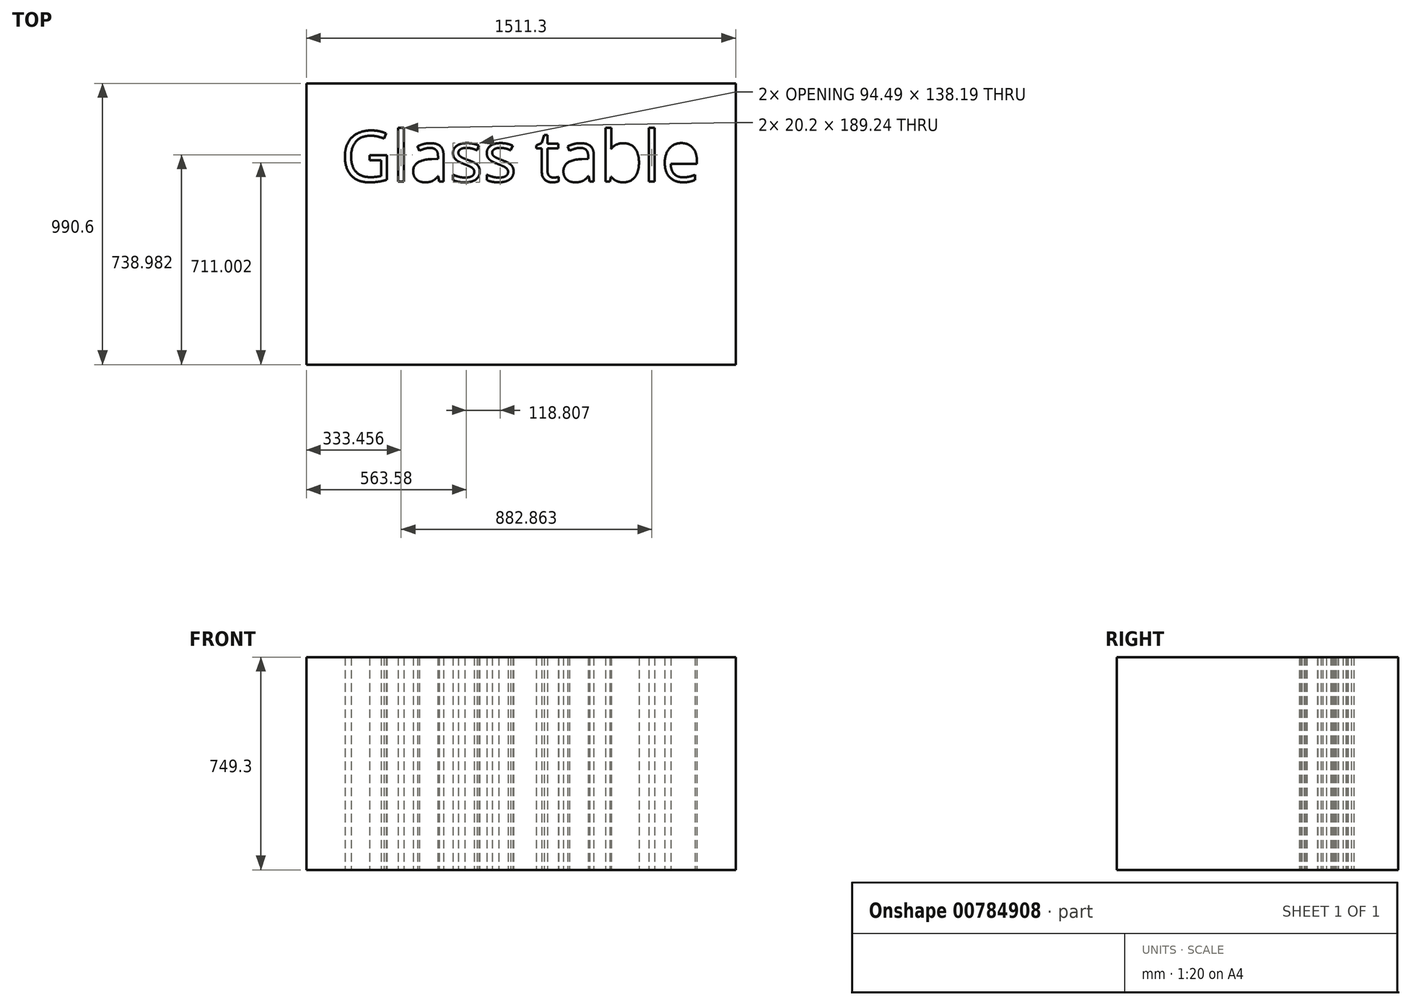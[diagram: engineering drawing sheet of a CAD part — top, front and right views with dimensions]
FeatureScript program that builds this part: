
annotation { "Feature Type Name" : "Feature", "Feature Type Description" : "" }
export const myFeature = defineFeature(function(context is Context, id is Id, definition is map)
    precondition{}
    {
        {
            var Q0;
            Q0=qCreatedBy(makeId("Top.planeOp"),FACE);
            var sketch = newSketch(context, id + "F0", { "sketchPlane" : qUnion([Q0])});
            skLineSegment(sketch, "E0.bottom", {"start": v(755.65, 495.3) * mm, "end": v(-755.65, 495.3) * mm});
            skLineSegment(sketch, "E0.top", {"start": v(755.65, -495.3) * mm, "end": v(-755.65, -495.3) * mm});
            skLineSegment(sketch, "E0.left", {"start": v(755.65, 495.3) * mm, "end": v(755.65, -495.3) * mm});
            skLineSegment(sketch, "E0.right", {"start": v(-755.65, 495.3) * mm, "end": v(-755.65, -495.3) * mm});
            skPoint(sketch, "E0.middle", {"position": v(0, 0) * mm});
            skText(sketch, "E1", { "text": "Glass table", "fontName": "OpenSans-Regular.ttf"});
            const initialGuessF0  = {"E1": [-0.635, 0.14906, 1, 0, 0.17932]};
            skSetInitialGuess(sketch, initialGuessF0);
            skSolve(sketch);
        }
        {
            var Q0;
            Q0=makeQuery(id+"F0.imprint","IMPRINT",FACE,{"disambiguationData":[TD([[makeQuery(id+"F0.imprint","IMPRINT",EDGE,{"derivedFrom":sQuery(id+"F0.wireOp",EDGE,"E0.bottom")}),1.0]])]});
            extrude(context, id + "F1", {"entities" : qUnion([Q0]), "depth" : 749.3 * mm, "offsetDistance" : 25.4 * mm});
        }
    });
